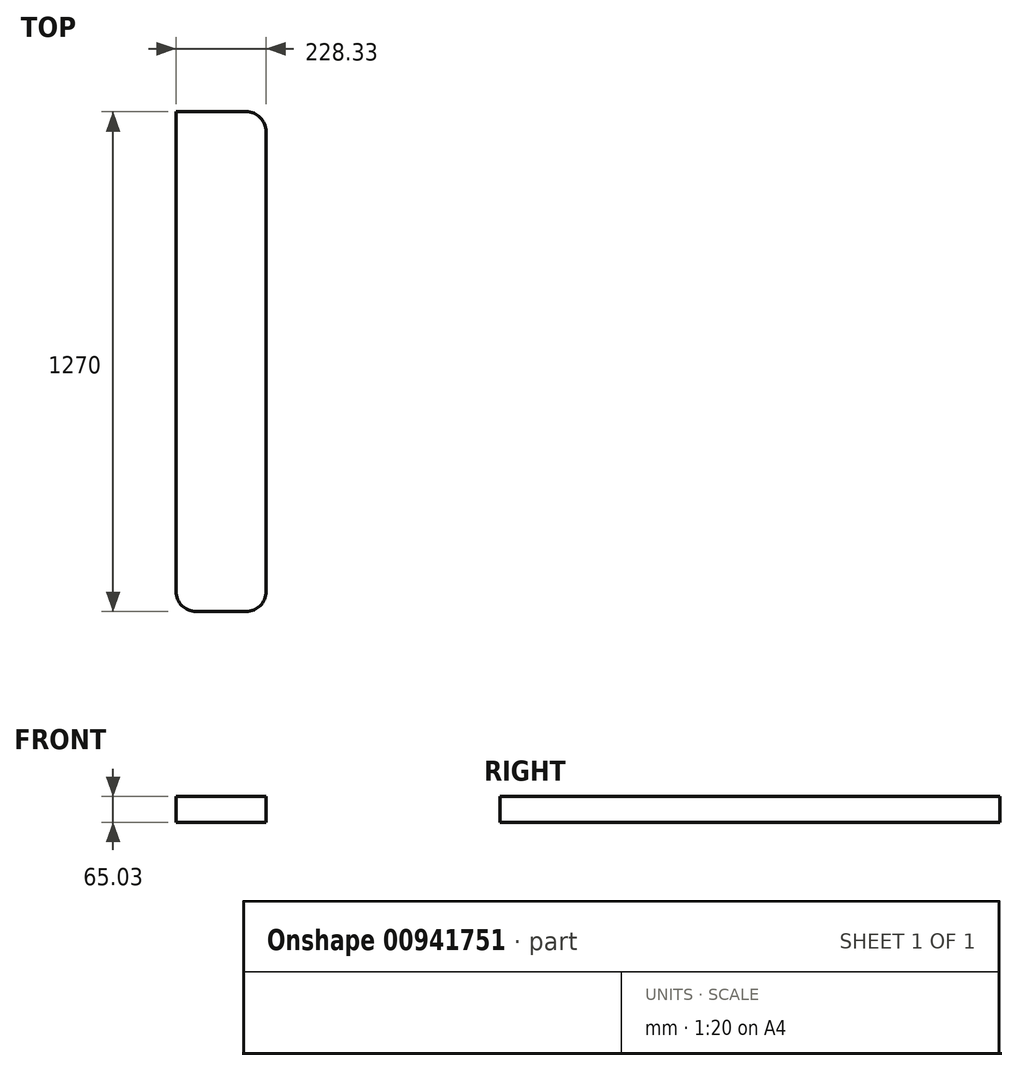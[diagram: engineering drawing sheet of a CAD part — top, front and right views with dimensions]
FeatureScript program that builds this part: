
annotation { "Feature Type Name" : "Feature", "Feature Type Description" : "" }
export const myFeature = defineFeature(function(context is Context, id is Id, definition is map)
    precondition{}
    {
        {
            var Q0;
            Q0=qCreatedBy(makeId("Front.planeOp"),FACE);
            var sketch = newSketch(context, id + "F0", { "sketchPlane" : qUnion([Q0])});
            skLineSegment(sketch, "E0.bottom", {"start": v(-121.47, 37.44) * mm, "end": v(106.86, 37.44) * mm});
            skLineSegment(sketch, "E0.top", {"start": v(-121.47, -27.59) * mm, "end": v(106.86, -27.59) * mm});
            skLineSegment(sketch, "E0.left", {"start": v(-121.47, 37.44) * mm, "end": v(-121.47, -27.59) * mm});
            skLineSegment(sketch, "E0.right", {"start": v(106.86, 37.44) * mm, "end": v(106.86, -27.59) * mm});
            skSolve(sketch);
        }
        {
            var Q0;
            Q0 = qSketchRegion(id + "F0", true);
            extrude(context, id + "F1", {"entities" : qUnion([Q0]), "depth" : 1270 * mm, "offsetDistance" : 25.4 * mm});
        }
        {
            var Q0;
            Q0=makeQuery(id+"F1.opExtrude","CAP_EDGE",EDGE,{"disambiguationData":[OSD([sQuery(id+"F0.wireOp",EDGE,"E0.left")])],"isStart":false});
            var Q1;
            Q1=makeQuery(id+"F1.opExtrude","CAP_EDGE",EDGE,{"disambiguationData":[OSD([sQuery(id+"F0.wireOp",EDGE,"E0.right")])],"isStart":false});
            var Q2;
            Q2=makeQuery(id+"F1.opExtrude","CAP_EDGE",EDGE,{"disambiguationData":[OSD([sQuery(id+"F0.wireOp",EDGE,"E0.right")])],"isStart":true});
            fillet(context, id + "F2", {"entities" : qUnion([Q0, Q1, Q2]), "tangentPropagation" : true, "radius" : 50.8 * mm, "defaultsChanged" : true, "vertexSettings" : [], "allowEdgeOverflow" : false});
        }
    });
